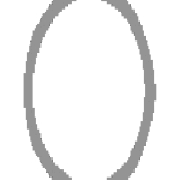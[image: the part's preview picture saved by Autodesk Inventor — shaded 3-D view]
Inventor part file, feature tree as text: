
AUTODESK INVENTOR PART (.ipt)
format: ipt  version: 2021 (Build 250183000, 183)  size: 112,640 bytes
history: native  units: in
note: dims shown in document units (in); Inventor stores cm internally (conversion verified against a paired STEP export)
features: other x4, sketch x3, plane x1
ambient origin geometry x8: Origin, YZ Plane, XZ Plane, XY Plane, X Axis, Y Axis, Z Axis, Center Point
bodies: Solid1 (feature_tree), Body (feature_tree)
feature tree (8):
  other  "Driven Length"
  other  "Frame Generator"
  other  "Start Plane"
  other  "End Plane"
  sketch  "Sketch"  dims[d2=18.4803in d4=-0.0in d5=18.4803in d6=0.12in d7=0.0in d8=90.0deg d9=18.4803in]
  sketch  "Sketch2"  dims[d0=1.0in]
  plane  "Work Plane3"
  sketch  "Sketch3"  dims[d1=0.065in]
